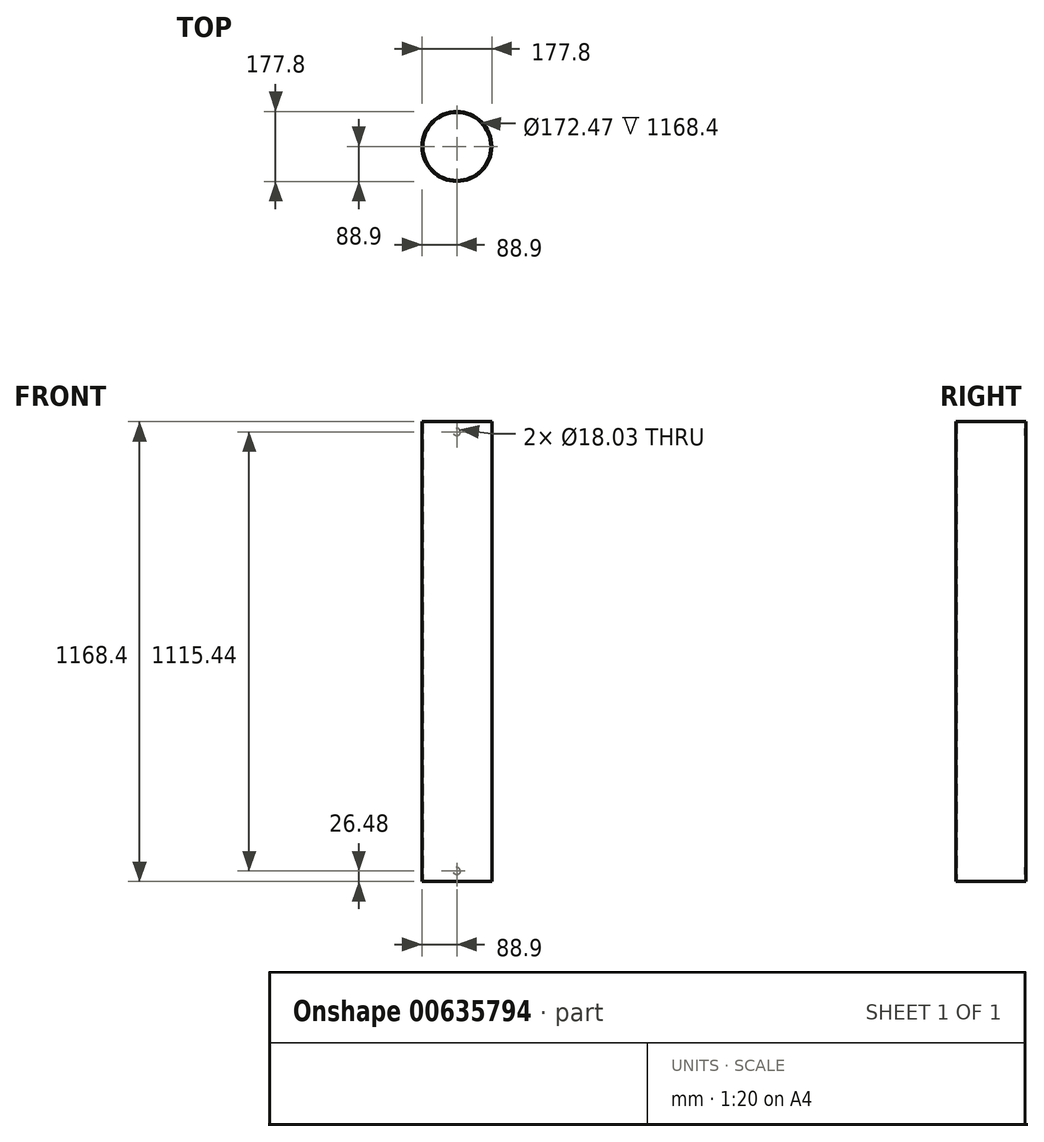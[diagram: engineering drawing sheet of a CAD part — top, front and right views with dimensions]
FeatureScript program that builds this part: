
annotation { "Feature Type Name" : "Feature", "Feature Type Description" : "" }
export const myFeature = defineFeature(function(context is Context, id is Id, definition is map)
    precondition{}
    {
        {
            var Q0;
            Q0=qCreatedBy(makeId("Top.planeOp"),FACE);
            var sketch = newSketch(context, id + "F0", { "sketchPlane" : qUnion([Q0])});
            skCircle(sketch, "E0", {"center": v(0, 0) * mm, "radius": 88.9 * mm});
            skCircle(sketch, "E1", {"center": v(0, 0) * mm, "radius": 86.23 * mm});
            skSolve(sketch);
        }
        {
            var Q0;
            Q0=qSketchRegion(id+"F0",true);
            extrude(context, id + "F1", {"entities" : qUnion([Q0]), "depth" : 1168.4 * mm, "offsetDistance" : 25.4 * mm});
        }
        {
            var Q0;
            Q0=qCreatedBy(makeId("Front.planeOp"),FACE);
            var sketch = newSketch(context, id + "F2", { "sketchPlane" : qUnion([Q0])});
            skCircle(sketch, "E2", {"center": v(0, 1141.92) * mm, "radius": 9.02 * mm});
            skCircle(sketch, "E3", {"center": v(0, 26.48) * mm, "radius": 9.02 * mm});
            skSolve(sketch);
        }
        {
            var Q0;
            Q0=qSketchRegion(id+"F2",true);
            extrude(context, id + "F3", {"entities" : qUnion([Q0]), "operationType" : NewBodyOperationType.REMOVE, "oppositeDirection" : true, "depth" : 203.2 * mm, "offsetDistance" : 25.4 * mm});
        }
    });
